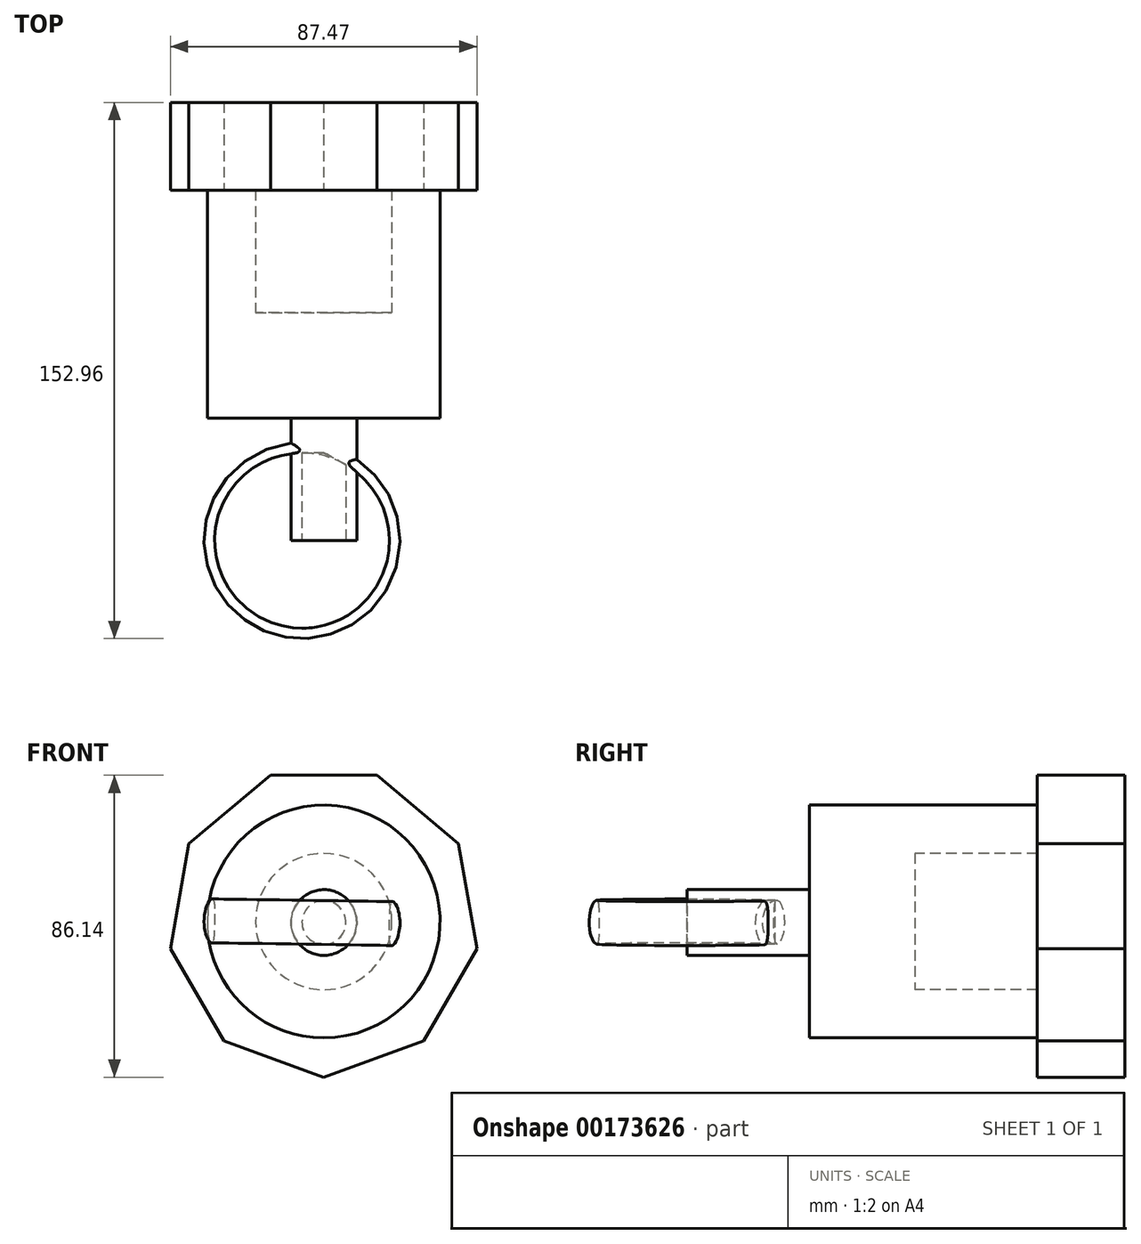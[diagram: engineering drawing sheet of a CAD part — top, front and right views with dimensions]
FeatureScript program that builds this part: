
annotation { "Feature Type Name" : "Feature", "Feature Type Description" : "" }
export const myFeature = defineFeature(function(context is Context, id is Id, definition is map)
    precondition{}
    {
        {
            var Q0;
            Q0=qCreatedBy(makeId("Front.planeOp"),FACE);
            var sketch = newSketch(context, id + "F0", { "sketchPlane" : qUnion([Q0])});
            skCircle(sketch, "E0", {"center": v(-48.3, 33.43) * mm, "radius": 17.74 * mm});
            skSolve(sketch);
        }
        {
            var Q0;
            Q0 = qSketchRegion(id + "F0", true);
            extrude(context, id + "F1", {"entities" : qUnion([Q0]), "depth" : 25 * mm});
        }
        {
            var Q0;
            Q0=makeQuery(id+"F1.opExtrude","CAP_FACE",FACE,{"disambiguationData":[OSD([sQuery(id+"F0.wireOp",EDGE,"E0")])],"isStart":false});
            var sketch = newSketch(context, id + "F2", { "sketchPlane" : qUnion([Q0])});
            skCircle(sketch, "E1", {"center": v(-48.3, 33.43) * mm, "radius": 9.38 * mm});
            skSolve(sketch);
        }
        {
            var Q0;
            Q0=makeQuery(id+"F2.imprint","IMPRINT",FACE,{"disambiguationData":[TD([[makeQuery(id+"F2.imprint","IMPRINT",EDGE,{"derivedFrom":sQuery(id+"F2.wireOp",EDGE,"E1")}),1.0]])]});
            extrude(context, id + "F3", {"entities" : qUnion([Q0]), "operationType" : NewBodyOperationType.ADD, "depth" : 40 * mm});
        }
        {
            var Q0;
            Q0=makeQuery(id+"F3.opExtrude","CAP_FACE",FACE,{"disambiguationData":[OSD([sQuery(id+"F2.wireOp",EDGE,"E1")])],"isStart":false});
            var sketch = newSketch(context, id + "F4", { "sketchPlane" : qUnion([Q0])});
            skCircle(sketch, "E2", {"center": v(-48.3, 33.43) * mm, "radius": 6.26 * mm});
            skSolve(sketch);
        }
        {
            var Q0;
            Q0 = qSketchRegion(id + "F4", true);
            extrude(context, id + "F5", {"entities" : qUnion([Q0]), "operationType" : NewBodyOperationType.REMOVE, "oppositeDirection" : true, "depth" : 25 * mm});
        }
        {
            var Q0;
            Q0=makeQuery(id+"F3.opExtrude","CAP_FACE",FACE,{"disambiguationData":[OSD([sQuery(id+"F2.wireOp",EDGE,"E1")])],"isStart":false});
            var sketch = newSketch(context, id + "F6", { "sketchPlane" : qUnion([Q0])});
            skLineSegment(sketch, "E3", {"start": v(-54.25, 54.1) * mm, "end": v(-54.85, 13.57) * mm});
            skLineSegment(sketch, "E4", {"start": v(-54.85, 13.57) * mm, "end": v(-21.96, 13.08) * mm});
            skLineSegment(sketch, "E5", {"start": v(-21.96, 13.08) * mm, "end": v(-54.25, 54.1) * mm});
            skSolve(sketch);
        }
        {
            var Q0;
            Q0=makeQuery(id+"F5.boolean.opBoolean","COPY",FACE,{"derivedFrom":makeQuery(id+"F5.opExtrude","CAP_FACE",FACE,{"disambiguationData":[OSD([sQuery(id+"F4.wireOp",EDGE,"E2")])],"isStart":false})});
            var Q1;
            Q1=sQuery(id+"F6.wireOp",EDGE,"E3");
            revolve(context, id + "F7", {"operationType" : NewBodyOperationType.ADD, "entities" : qUnion([Q0]), "axis" : qUnion([Q1]), "revolveType" : RevolveType.FULL});
        }
        {
            var Q0;
            Q0=qCreatedBy(makeId("Front.planeOp"),FACE);
            var sketch = newSketch(context, id + "F8", { "sketchPlane" : qUnion([Q0])});
            skCircle(sketch, "E6", {"center": v(-48.36, 33.7) * mm, "radius": 33.21 * mm});
            skSolve(sketch);
        }
        {
            var Q0;
            Q0=makeQuery(id+"F8.imprint","IMPRINT",FACE,{"disambiguationData":[TD([[makeQuery(id+"F8.imprint","IMPRINT",EDGE,{"derivedFrom":sQuery(id+"F8.wireOp",EDGE,"E6")}),1.0]])]});
            extrude(context, id + "F9", {"entities" : qUnion([Q0]), "operationType" : NewBodyOperationType.ADD, "depth" : 30 * mm});
        }
        {
            var Q0;
            Q0=makeQuery(id+"F9.boolean.opBoolean","MERGE",FACE,{"derivedFrom":[makeQuery(id+"F1.opExtrude","CAP_FACE",FACE,{"disambiguationData":[OSD([sQuery(id+"F0.wireOp",EDGE,"E0")])],"isStart":true}),makeQuery(id+"F9.opExtrude","CAP_FACE",FACE,{"disambiguationData":[OSD([sQuery(id+"F8.wireOp",EDGE,"E6")])],"isStart":true})]});
            var sketch = newSketch(context, id + "F10", { "sketchPlane" : qUnion([Q0])});
            skCircle(sketch, "E7", {"center": v(48.36, 33.7) * mm, "radius": 19.45 * mm});
            skLineSegment(sketch, "E8", {"start": v(27.41, 59.48) * mm, "end": v(36.38, 49.03) * mm});
            skLineSegment(sketch, "E9", {"start": v(60.35, 49.03) * mm, "end": v(69.65, 59.2) * mm});
            skLineSegment(sketch, "E10", {"start": v(36.38, 18.39) * mm, "end": v(27.76, 7.66) * mm});
            skLineSegment(sketch, "E11", {"start": v(60.35, 18.39) * mm, "end": v(68.97, 7.66) * mm});
            skSolve(sketch);
        }
        {
            var Q0;
            {var subQ0=sQuery(id+"F10.wireOp",EDGE,"E8");Q0=makeQuery(id+"F10.imprint","IMPRINT",FACE,{"disambiguationData":[TD([[makeQuery(id+"F10.imprint","IMPRINT",EDGE,{"derivedFrom":subQ0}),1.0]])]});}
            var Q1;
            {var subQ0=sQuery(id+"F10.wireOp",EDGE,"E9");Q1=makeQuery(id+"F10.imprint","IMPRINT",FACE,{"disambiguationData":[TD([[makeQuery(id+"F10.imprint","IMPRINT",EDGE,{"derivedFrom":subQ0}),-1.0]])]});}
            var Q2;
            {var subQ0=sQuery(id+"F10.wireOp",EDGE,"E10");Q2=makeQuery(id+"F10.imprint","IMPRINT",FACE,{"disambiguationData":[TD([[makeQuery(id+"F10.imprint","IMPRINT",EDGE,{"derivedFrom":subQ0}),1.0]])]});}
            var Q3;
            {var subQ0=sQuery(id+"F10.wireOp",EDGE,"E8");Q3=makeQuery(id+"F10.imprint","IMPRINT",FACE,{"disambiguationData":[TD([[makeQuery(id+"F10.imprint","IMPRINT",EDGE,{"derivedFrom":subQ0}),-1.0]])]});}
            extrude(context, id + "F11", {"entities" : qUnion([Q0, Q1, Q2, Q3]), "operationType" : NewBodyOperationType.ADD, "depth" : 35 * mm});
        }
        {
            var Q0;
            Q0=makeQuery(id+"F11.opExtrude","CAP_FACE",FACE,{"disambiguationData":[OSD([sQuery(id+"F8.wireOp",EDGE,"E6"),sQuery(id+"F10.wireOp",EDGE,"E7")])],"isStart":false});
            var sketch = newSketch(context, id + "F12", { "sketchPlane" : qUnion([Q0])});
            skCircle(sketch, "E12.cCircle", {"center": v(48.36, 33.7) * mm, "radius": 41.73 * mm, "construction": true});
            skLineSegment(sketch, "E12.0", {"start": v(33.18, 75.44) * mm, "end": v(63.55, 75.44) * mm});
            skLineSegment(sketch, "E12.1", {"start": v(63.55, 75.44) * mm, "end": v(86.82, 55.91) * mm});
            skLineSegment(sketch, "E12.2", {"start": v(86.82, 55.91) * mm, "end": v(92.1, 26) * mm});
            skLineSegment(sketch, "E12.3", {"start": v(92.1, 26) * mm, "end": v(76.91, -0.31) * mm});
            skLineSegment(sketch, "E12.4", {"start": v(76.91, -0.31) * mm, "end": v(48.36, -10.7) * mm});
            skLineSegment(sketch, "E12.5", {"start": v(48.36, -10.7) * mm, "end": v(19.82, -0.31) * mm});
            skLineSegment(sketch, "E12.6", {"start": v(19.82, -0.31) * mm, "end": v(4.63, 26) * mm});
            skLineSegment(sketch, "E12.7", {"start": v(4.63, 26) * mm, "end": v(9.9, 55.91) * mm});
            skLineSegment(sketch, "E12.8", {"start": v(9.9, 55.91) * mm, "end": v(33.18, 75.44) * mm});
            skPoint(sketch, "E12.0.midPoint", {"position": v(48.36, 75.44) * mm});
            skSolve(sketch);
        }
        {
            var Q0;
            Q0 = qSketchRegion(id + "F12", true);
            extrude(context, id + "F13", {"entities" : qUnion([Q0]), "operationType" : NewBodyOperationType.ADD, "depth" : 25 * mm});
        }
    });
